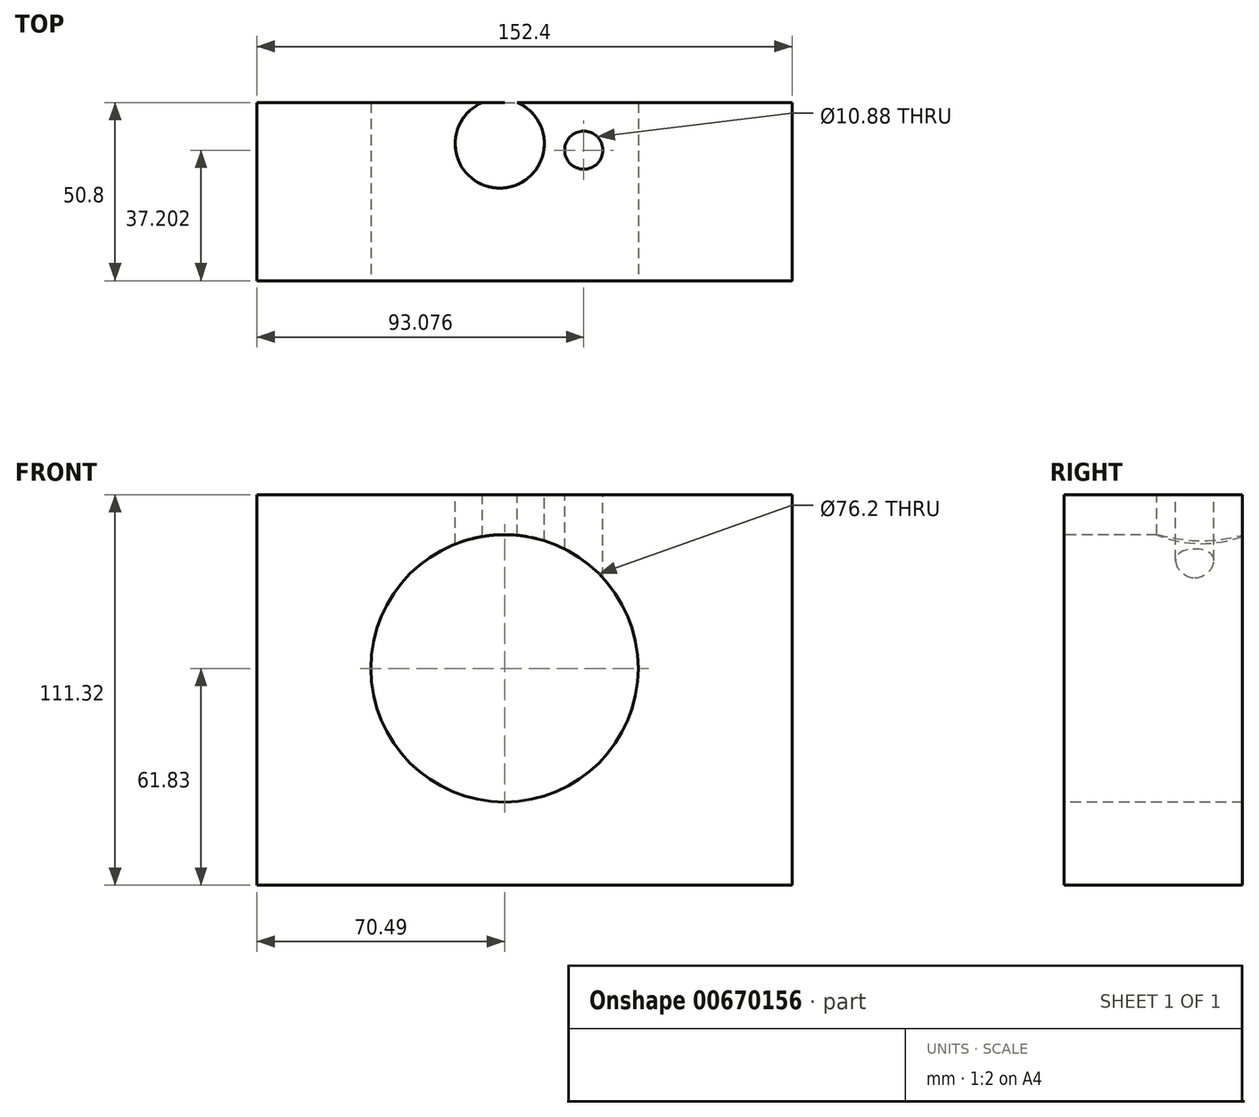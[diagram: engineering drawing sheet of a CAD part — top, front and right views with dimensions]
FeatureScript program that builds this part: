
annotation { "Feature Type Name" : "Feature", "Feature Type Description" : "" }
export const myFeature = defineFeature(function(context is Context, id is Id, definition is map)
    precondition{}
    {
        {
            var Q0;
            Q0=qCreatedBy(makeId("Front.planeOp"),FACE);
            var sketch = newSketch(context, id + "F0", { "sketchPlane" : qUnion([Q0])});
            skLineSegment(sketch, "E0.bottom", {"start": v(-70.49, 49.5) * mm, "end": v(81.91, 49.5) * mm});
            skLineSegment(sketch, "E0.top", {"start": v(-70.49, -61.83) * mm, "end": v(81.91, -61.83) * mm});
            skLineSegment(sketch, "E0.left", {"start": v(-70.49, 49.5) * mm, "end": v(-70.49, -61.83) * mm});
            skLineSegment(sketch, "E0.right", {"start": v(81.91, 49.5) * mm, "end": v(81.91, -61.83) * mm});
            skSolve(sketch);
        }
        {
            var Q0;
            Q0 = qSketchRegion(id + "F0", true);
            extrude(context, id + "F1", {"entities" : qUnion([Q0]), "depth" : 25.4 * mm, "offsetDistance" : 25.4 * mm, "hasSecondDirection" : true, "secondDirectionOppositeDirection" : true, "secondDirectionDepth" : 25.4 * mm});
        }
        {
            var Q0;
            Q0=makeQuery(id+"F1.opExtrude","CAP_FACE",FACE,{"disambiguationData":[OSD([sQuery(id+"F0.wireOp",EDGE,"E0.bottom"),sQuery(id+"F0.wireOp",EDGE,"E0.top"),sQuery(id+"F0.wireOp",EDGE,"E0.left"),sQuery(id+"F0.wireOp",EDGE,"E0.right")])],"isStart":false});
            var sketch = newSketch(context, id + "F2", { "sketchPlane" : qUnion([Q0])});
            skCircle(sketch, "E1", {"center": v(0, 0) * mm, "radius": 38.1 * mm});
            skSolve(sketch);
        }
        {
            var Q0;
            Q0 = qSketchRegion(id + "F2", true);
            extrude(context, id + "F3", {"entities" : qUnion([Q0]), "operationType" : NewBodyOperationType.REMOVE, "endBound" : BoundingType.THROUGH_ALL, "oppositeDirection" : true, "depth" : 25.4 * mm, "offsetDistance" : 25.4 * mm});
        }
        {
            var Q0;
            Q0=makeQuery(id+"F1.opExtrude","SWEPT_FACE",FACE,{"disambiguationData":[OSD([sQuery(id+"F0.wireOp",EDGE,"E0.bottom")])]});
            var sketch = newSketch(context, id + "F4", { "sketchPlane" : qUnion([Q0])});
            skCircle(sketch, "E2", {"center": v(-1.35, 13.69) * mm, "radius": 12.7 * mm});
            skCircle(sketch, "E3", {"center": v(22.59, 11.8) * mm, "radius": 5.44 * mm});
            skSolve(sketch);
        }
        {
            var Q0;
            Q0 = qSketchRegion(id + "F4", true);
            extrude(context, id + "F5", {"entities" : qUnion([Q0]), "operationType" : NewBodyOperationType.REMOVE, "oppositeDirection" : true, "depth" : 25.4 * mm, "offsetDistance" : 25.4 * mm});
        }
    });
